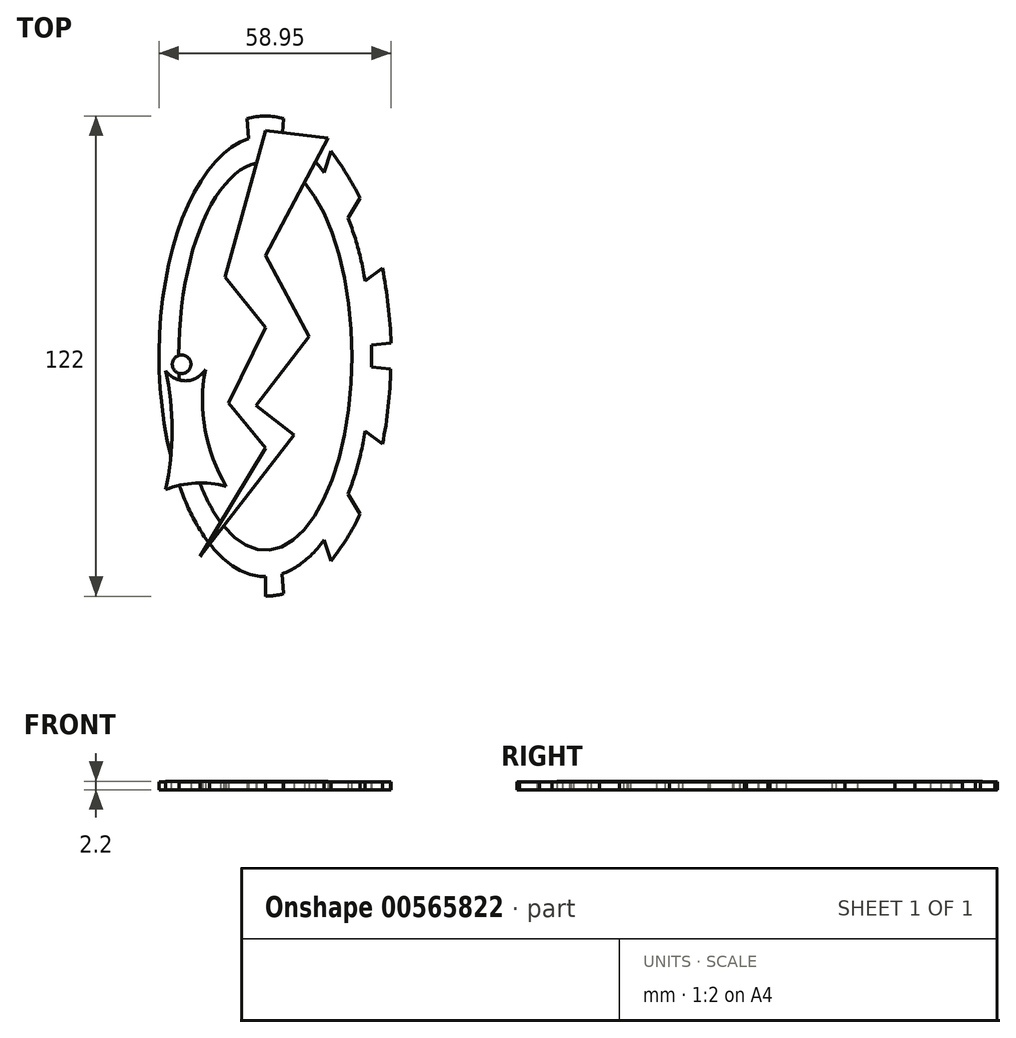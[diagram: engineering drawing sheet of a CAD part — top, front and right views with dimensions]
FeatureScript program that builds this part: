
annotation { "Feature Type Name" : "Feature", "Feature Type Description" : "" }
export const myFeature = defineFeature(function(context is Context, id is Id, definition is map)
    precondition{}
    {
        {
            var Q0;
            Q0=qCreatedBy(makeId("Top.planeOp"),FACE);
            var sketch = newSketch(context, id + "F0", { "sketchPlane" : qUnion([Q0])});
            skEllipse(sketch, "E0", {"center": v(0, 0) * mm, "majorRadius": 61 * mm, "minorRadius": 32 * mm, "majorAxis": v(0, 1), "construction": true});
            skEllipse(sketch, "E1", {"center": v(0, 0) * mm, "majorRadius": 56 * mm, "minorRadius": 27 * mm, "majorAxis": v(0, 1)});
            skEllipse(sketch, "E2", {"center": v(0, 0) * mm, "majorRadius": 49.32 * mm, "minorRadius": 22 * mm, "majorAxis": v(0, 1)});
            skLineSegment(sketch, "E3", {"start": v(0, 0) * mm, "end": v(0, 67.16) * mm, "construction": true});
            skPoint(sketch, "E3.endSnap0", {"position": v(0, 61) * mm});
            skLineSegment(sketch, "E4", {"start": v(0, 0) * mm, "end": v(60.02, 0) * mm, "construction": true});
            skLineSegment(sketch, "E5", {"start": v(0, 0) * mm, "end": v(5.26, 67.94) * mm, "construction": true});
            skLineSegment(sketch, "E6.MirrorCS", {"start": v(0, 0) * mm, "end": v(10.34, 66.36) * mm, "construction": true});
            skLineSegment(sketch, "E7.MirrorCS", {"start": v(0, 0) * mm, "end": v(15.66, 66.32) * mm, "construction": true});
            skLineSegment(sketch, "E8.MirrorCS", {"start": v(0, 0) * mm, "end": v(20.43, 63.97) * mm, "construction": true});
            skLineSegment(sketch, "E9.MirrorCS", {"start": v(0, 0) * mm, "end": v(25.68, 63.12) * mm, "construction": true});
            skLineSegment(sketch, "E10.MirrorCS", {"start": v(0, 0) * mm, "end": v(30.04, 60.07) * mm, "construction": true});
            skLineSegment(sketch, "E11.MirrorCS", {"start": v(0, 0) * mm, "end": v(35.1, 58.41) * mm, "construction": true});
            skLineSegment(sketch, "E12.MirrorCS", {"start": v(0, 0) * mm, "end": v(38.93, 54.72) * mm, "construction": true});
            skLineSegment(sketch, "E13.MirrorCS", {"start": v(0, 0) * mm, "end": v(43.67, 52.31) * mm, "construction": true});
            skLineSegment(sketch, "E14.MirrorCS", {"start": v(0, 0) * mm, "end": v(46.9, 48.08) * mm, "construction": true});
            skLineSegment(sketch, "E15.MirrorCS", {"start": v(0, 0) * mm, "end": v(51.2, 44.97) * mm, "construction": true});
            skLineSegment(sketch, "E16.MirrorCS", {"start": v(0, 0) * mm, "end": v(53.73, 40.28) * mm, "construction": true});
            skLineSegment(sketch, "E17.MirrorCS", {"start": v(0, 0) * mm, "end": v(57.52, 36.55) * mm, "construction": true});
            skLineSegment(sketch, "E18.MirrorCS", {"start": v(0, 0) * mm, "end": v(59.3, 31.53) * mm, "construction": true});
            skLineSegment(sketch, "E19.MirrorCS", {"start": v(0, 0) * mm, "end": v(62.46, 27.25) * mm, "construction": true});
            skLineSegment(sketch, "E20.MirrorCS", {"start": v(0, 0) * mm, "end": v(63.44, 22.03) * mm, "construction": true});
            skLineSegment(sketch, "E21.MirrorCS", {"start": v(0, 0) * mm, "end": v(65.91, 17.31) * mm, "construction": true});
            skLineSegment(sketch, "E22.MirrorCS", {"start": v(0, 0) * mm, "end": v(66.08, 12) * mm, "construction": true});
            skLineSegment(sketch, "E23.MirrorCS", {"start": v(0, 0) * mm, "end": v(67.8, 6.96) * mm, "construction": true});
            skLineSegment(sketch, "E24.MirrorCS", {"start": v(0, 0) * mm, "end": v(67.8, -6.96) * mm, "construction": true});
            skLineSegment(sketch, "E25.MirrorCS", {"start": v(0, 0) * mm, "end": v(66.08, -12) * mm, "construction": true});
            skLineSegment(sketch, "E26.MirrorCS", {"start": v(0, 0) * mm, "end": v(65.91, -17.31) * mm, "construction": true});
            skLineSegment(sketch, "E27.MirrorCS", {"start": v(0, 0) * mm, "end": v(63.44, -22.03) * mm, "construction": true});
            skLineSegment(sketch, "E28.MirrorCS", {"start": v(0, 0) * mm, "end": v(62.46, -27.25) * mm, "construction": true});
            skLineSegment(sketch, "E29.MirrorCS", {"start": v(0, 0) * mm, "end": v(59.3, -31.53) * mm, "construction": true});
            skLineSegment(sketch, "E30.MirrorCS", {"start": v(0, 0) * mm, "end": v(57.52, -36.55) * mm, "construction": true});
            skLineSegment(sketch, "E31.MirrorCS", {"start": v(0, 0) * mm, "end": v(53.73, -40.28) * mm, "construction": true});
            skLineSegment(sketch, "E32.MirrorCS", {"start": v(0, 0) * mm, "end": v(51.2, -44.97) * mm, "construction": true});
            skLineSegment(sketch, "E33.MirrorCS", {"start": v(0, 0) * mm, "end": v(46.9, -48.08) * mm, "construction": true});
            skLineSegment(sketch, "E34.MirrorCS", {"start": v(0, 0) * mm, "end": v(43.67, -52.31) * mm, "construction": true});
            skLineSegment(sketch, "E35.MirrorCS", {"start": v(0, 0) * mm, "end": v(38.93, -54.72) * mm, "construction": true});
            skLineSegment(sketch, "E36.MirrorCS", {"start": v(0, 0) * mm, "end": v(35.1, -58.41) * mm, "construction": true});
            skLineSegment(sketch, "E37.MirrorCS", {"start": v(0, 0) * mm, "end": v(30.04, -60.07) * mm, "construction": true});
            skLineSegment(sketch, "E38.MirrorCS", {"start": v(0, 0) * mm, "end": v(25.68, -63.12) * mm, "construction": true});
            skLineSegment(sketch, "E39.MirrorCS", {"start": v(0, 0) * mm, "end": v(20.43, -63.97) * mm, "construction": true});
            skLineSegment(sketch, "E40.MirrorCS", {"start": v(0, 0) * mm, "end": v(15.66, -66.32) * mm, "construction": true});
            skLineSegment(sketch, "E41.MirrorCS", {"start": v(0, 0) * mm, "end": v(10.34, -66.36) * mm, "construction": true});
            skLineSegment(sketch, "E42.MirrorCS", {"start": v(0, 0) * mm, "end": v(5.26, -67.94) * mm, "construction": true});
            skLineSegment(sketch, "E43.MirrorCS", {"start": v(0, 0) * mm, "end": v(0, -67.16) * mm, "construction": true});
            skLineSegment(sketch, "E44.MirrorCS", {"start": v(0, 0) * mm, "end": v(-5.26, 67.94) * mm, "construction": true});
            skLineSegment(sketch, "E45", {"start": v(-4.28, 55.3) * mm, "end": v(-4.67, 60.35) * mm});
            skLineSegment(sketch, "E46", {"start": v(4.28, 55.3) * mm, "end": v(4.67, 60.35) * mm});
            skArc(sketch, "E47", {"start": v(4.67, 60.35) * mm, "mid": v(0, 61) * mm, "end": v(-4.67, 60.35) * mm});
            skLineSegment(sketch, "E48", {"start": v(26.97, 2.77) * mm, "end": v(31.95, 3.28) * mm});
            skLineSegment(sketch, "E49", {"start": v(25.4, 19.04) * mm, "end": v(29.78, 22.33) * mm});
            skArc(sketch, "E50", {"start": v(31.95, 3.28) * mm, "mid": v(31.23, 12.84) * mm, "end": v(29.78, 22.33) * mm});
            skLineSegment(sketch, "E51", {"start": v(21.06, 35.05) * mm, "end": v(24.1, 40.12) * mm});
            skLineSegment(sketch, "E52", {"start": v(14.91, 46.69) * mm, "end": v(16.64, 52.1) * mm});
            skArc(sketch, "E53", {"start": v(24.1, 40.12) * mm, "mid": v(20.64, 46.28) * mm, "end": v(16.64, 52.1) * mm});
            skLineSegment(sketch, "E54", {"start": v(26.97, -2.77) * mm, "end": v(31.86, -3.27) * mm});
            skLineSegment(sketch, "E55", {"start": v(25.4, -19.04) * mm, "end": v(29.78, -22.33) * mm});
            skArc(sketch, "E56", {"start": v(29.78, -22.33) * mm, "mid": v(31.22, -12.84) * mm, "end": v(31.86, -3.27) * mm});
            skLineSegment(sketch, "E57", {"start": v(21.06, -35.05) * mm, "end": v(24.1, -40.12) * mm});
            skLineSegment(sketch, "E58", {"start": v(14.91, -46.69) * mm, "end": v(16.64, -52.1) * mm});
            skArc(sketch, "E59", {"start": v(16.64, -52.1) * mm, "mid": v(20.72, -46.33) * mm, "end": v(24.1, -40.12) * mm});
            skLineSegment(sketch, "E60", {"start": v(4.28, -55.3) * mm, "end": v(4.67, -60.35) * mm});
            skLineSegment(sketch, "E61", {"start": v(0, -56) * mm, "end": v(0, -61) * mm});
            skArc(sketch, "E62", {"start": v(0, -61) * mm, "mid": v(2.36, -60.83) * mm, "end": v(4.67, -60.35) * mm});
            skSolve(sketch);
        }
        {
            var Q0;
            Q0=makeQuery(id+"F0.imprint","IMPRINT",FACE,{"disambiguationData":[TD([[makeQuery(id+"F0.imprint","IMPRINT",EDGE,{"derivedFrom":sQuery(id+"F0.wireOp",EDGE,"E2")}),-1.0]])]});
            var Q1;
            {var subQ0=sQuery(id+"F0.wireOp",EDGE,"E60");Q1=makeQuery(id+"F0.imprint","IMPRINT",FACE,{"disambiguationData":[TD([[makeQuery(id+"F0.imprint","IMPRINT",EDGE,{"derivedFrom":subQ0}),-1.0]])]});}
            var Q2;
            {var subQ0=sQuery(id+"F0.wireOp",EDGE,"E57");Q2=makeQuery(id+"F0.imprint","IMPRINT",FACE,{"disambiguationData":[TD([[makeQuery(id+"F0.imprint","IMPRINT",EDGE,{"derivedFrom":subQ0}),-1.0]])]});}
            var Q3;
            {var subQ0=sQuery(id+"F0.wireOp",EDGE,"E54");Q3=makeQuery(id+"F0.imprint","IMPRINT",FACE,{"disambiguationData":[TD([[makeQuery(id+"F0.imprint","IMPRINT",EDGE,{"derivedFrom":subQ0}),-1.0]])]});}
            var Q4;
            {var subQ0=sQuery(id+"F0.wireOp",EDGE,"E48");Q4=makeQuery(id+"F0.imprint","IMPRINT",FACE,{"disambiguationData":[TD([[makeQuery(id+"F0.imprint","IMPRINT",EDGE,{"derivedFrom":subQ0}),1.0]])]});}
            var Q5;
            {var subQ0=sQuery(id+"F0.wireOp",EDGE,"E51");Q5=makeQuery(id+"F0.imprint","IMPRINT",FACE,{"disambiguationData":[TD([[makeQuery(id+"F0.imprint","IMPRINT",EDGE,{"derivedFrom":subQ0}),1.0]])]});}
            var Q6;
            {var subQ0=sQuery(id+"F0.wireOp",EDGE,"E45");Q6=makeQuery(id+"F0.imprint","IMPRINT",FACE,{"disambiguationData":[TD([[makeQuery(id+"F0.imprint","IMPRINT",EDGE,{"derivedFrom":subQ0}),-1.0]])]});}
            extrude(context, id + "F1", {"entities" : qUnion([Q0, Q1, Q2, Q3, Q4, Q5, Q6]), "depth" : 2 * mm, "offsetDistance" : 25 * mm});
        }
        {
            var Q0;
            Q0=qCreatedBy(makeId("Top.planeOp"),FACE);
            var sketch = newSketch(context, id + "F2", { "sketchPlane" : qUnion([Q0])});
            skLineSegment(sketch, "E63", {"start": v(0, 57.25) * mm, "end": v(-10.2, 20.03) * mm});
            skLineSegment(sketch, "E64", {"start": v(-10.2, 20.03) * mm, "end": v(0, 7.3) * mm});
            skLineSegment(sketch, "E65", {"start": v(0, 7.3) * mm, "end": v(-9.38, -11.93) * mm});
            skLineSegment(sketch, "E66", {"start": v(-9.38, -11.93) * mm, "end": v(0, -23.4) * mm});
            skLineSegment(sketch, "E67", {"start": v(0, -23.4) * mm, "end": v(-16.58, -50.88) * mm});
            skLineSegment(sketch, "E68", {"start": v(-16.58, -50.88) * mm, "end": v(7.27, -19.98) * mm});
            skLineSegment(sketch, "E69", {"start": v(7.27, -19.98) * mm, "end": v(-2.41, -12.5) * mm});
            skLineSegment(sketch, "E70", {"start": v(-2.41, -12.5) * mm, "end": v(11.04, 4.93) * mm});
            skLineSegment(sketch, "E71", {"start": v(11.04, 4.93) * mm, "end": v(0, 25.52) * mm});
            skLineSegment(sketch, "E72", {"start": v(0, 25.52) * mm, "end": v(15.97, 55.42) * mm});
            skLineSegment(sketch, "E73", {"start": v(15.97, 55.42) * mm, "end": v(0, 57.25) * mm});
            skSolve(sketch);
        }
        {
            var Q0;
            Q0 = qSketchRegion(id + "F2", true);
            extrude(context, id + "F3", {"entities" : qUnion([Q0]), "operationType" : NewBodyOperationType.ADD, "depth" : 2.2 * mm, "offsetDistance" : 25 * mm});
        }
        {
            var Q0;
            Q0=qCreatedBy(makeId("Top.planeOp"),FACE);
            var sketch = newSketch(context, id + "F4", { "sketchPlane" : qUnion([Q0])});
            skArc(sketch, "E74", {"start": v(-25.4, -3.6) * mm, "mid": v(-20.28, -6.26) * mm, "end": v(-15.25, -3.43) * mm});
            skArc(sketch, "E75", {"start": v(-25.4, -33.94) * mm, "mid": v(-23.67, -18.77) * mm, "end": v(-25.4, -3.6) * mm});
            skArc(sketch, "E76", {"start": v(-15.25, -3.43) * mm, "mid": v(-15.27, -18.72) * mm, "end": v(-9.93, -33.06) * mm});
            skArc(sketch, "E77", {"start": v(-9.93, -33.06) * mm, "mid": v(-17.73, -32.26) * mm, "end": v(-25.4, -33.94) * mm});
            skSolve(sketch);
        }
        {
            var Q0;
            Q0 = qSketchRegion(id + "F4", true);
            extrude(context, id + "F5", {"entities" : qUnion([Q0]), "operationType" : NewBodyOperationType.ADD, "depth" : 2.2 * mm, "offsetDistance" : 25 * mm});
        }
        {
            var Q0;
            Q0=qCreatedBy(makeId("Top.planeOp"),FACE);
            var sketch = newSketch(context, id + "F6", { "sketchPlane" : qUnion([Q0])});
            skCircle(sketch, "E78", {"center": v(-21.28, -2.09) * mm, "radius": 2.36 * mm});
            skSolve(sketch);
        }
        {
            var Q0;
            Q0 = qSketchRegion(id + "F6", true);
            extrude(context, id + "F7", {"entities" : qUnion([Q0]), "operationType" : NewBodyOperationType.ADD, "depth" : 2.2 * mm, "offsetDistance" : 25 * mm});
        }
    });
